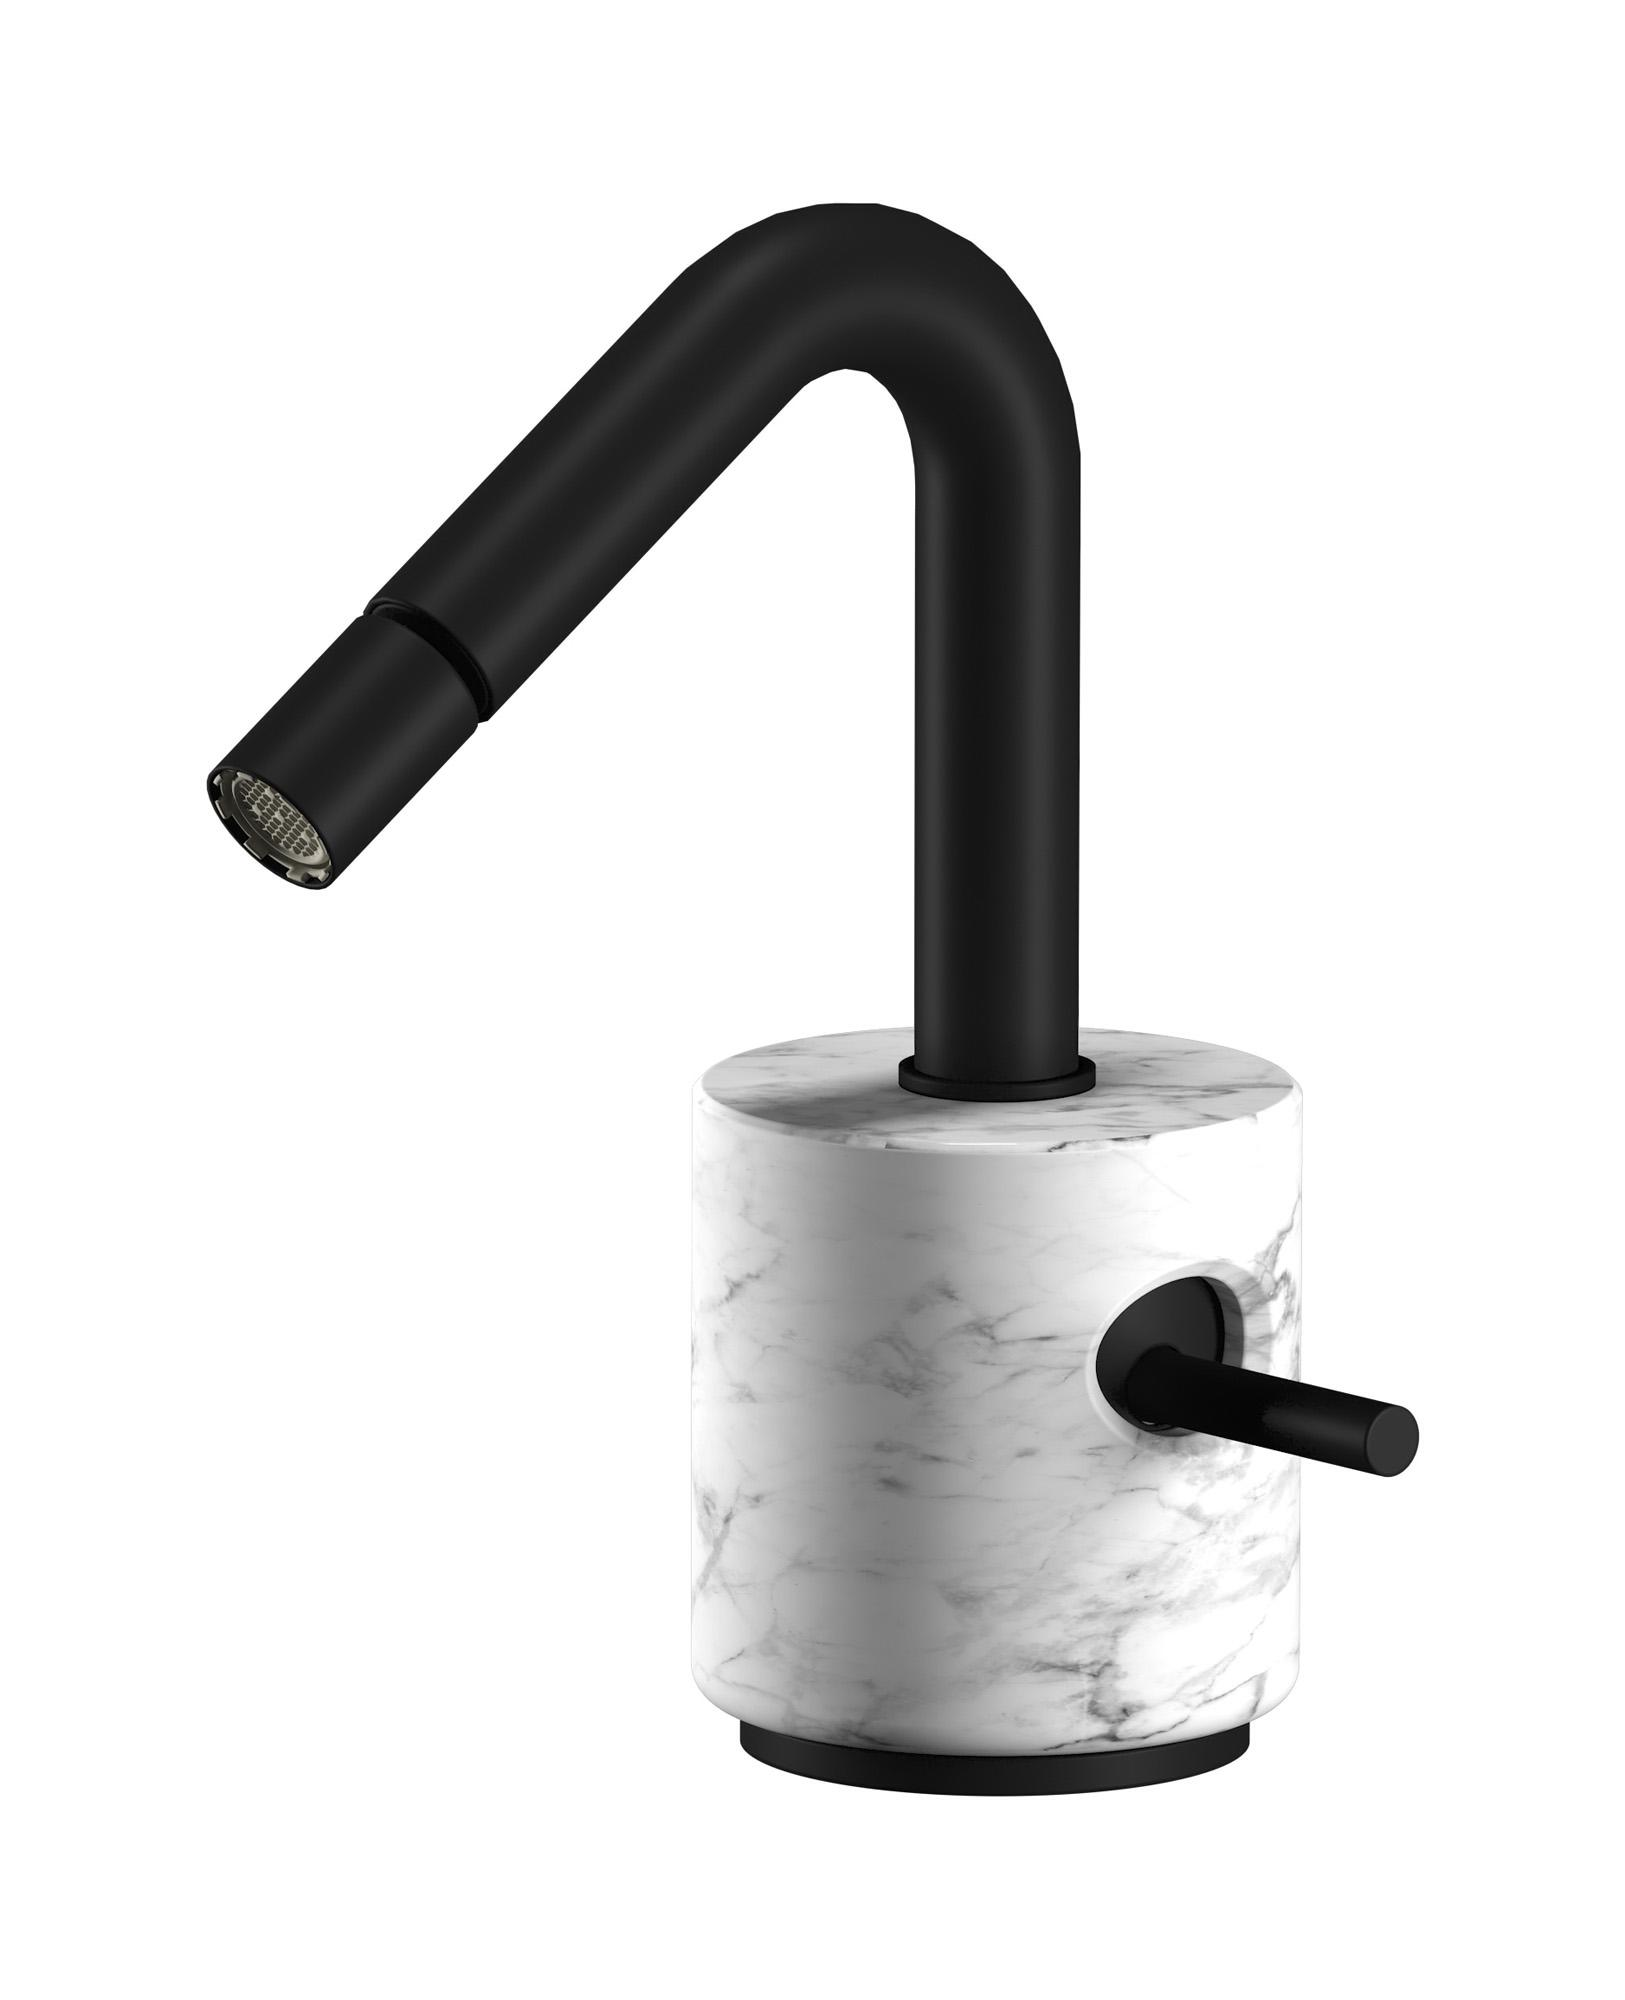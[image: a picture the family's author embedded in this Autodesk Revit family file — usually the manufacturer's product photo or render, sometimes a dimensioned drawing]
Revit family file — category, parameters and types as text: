
# Revit family: MR220_1
name_source: partatom
category: Apparecchi idraulici
units: mm (PartAtom-declared; Revit-internal decimal feet)

## family parameters
Basato su piano di lavoro = No
Condiviso = No
Mantieni orientamento annotazione = No
Numero OmniClass = 23.45.55.17
Punto di calcolo locali = No
Quota connettore circolare = Usa diametro
Sempre verticale = Sì
Taglio con vuoti quando caricato = No
Tipo di parte = Normale
Titolo OmniClass = Mixing Faucets

## types (14) — shared parameters
Cold water inlet = 10 mm  [stored 0.0328084 ft]
Commenti sul tipo = Bidet mixer
Connessione CW = No
Connessione HW = No
Connessione di scarico = No
Connessione di ventilazione = No
Descrizione = Monohole bidet mixer
Hot water inlet = 10 mm  [stored 0.0328084 ft]
Produttore = IB Rubinetterie S.p.A.
URL = https://www.weareib.it
zero-valued in all types: Prospetto di default

## per-type parameters (varying)
| type | Finishes surface | Immagine tipo | Modello |
| Chrome | IB_Chrome | MR220CC_1.jpg | MR220CC_1 |
| Platinum | IB_Platinum | MR220PL_1.jpg | MR220PL_1 |
| Brushed nickel | IB_Platinum | MR220SS_1.jpg | MR220SS_1 |
| Natural brass | IB_Brass | MR220ON_1.jpg | MR220ON_1 |
| Matt white | IB_matt white | MR220BO_1.jpg | MR220BO_1 |
| Matt black | IB_matt black | MR220NP_1.jpg | MR220NP_1 |
| Black chrome | IB_Black chrome | MR220CF_1.jpg | MR220CF_1 |
| Brushed black chrome | IB_Brushed black chrome | MR220CS_1.jpg | MR220CS_1 |
| Pale gold | IB_Pale gold | MR220II_1.jpg | MR220II_1 |
| Brushed pale gold | IB_brushed pale gold | MR220IS_1.jpg | MR220IS_1 |
| Rose gold | IB_Rose gold | MR220RS_1.jpg | MR220RS_1 |
| Brushed rose gold | IB_Brushed rose gold | MR220SR_1.jpg | MR220SR_1 |
| Gold | IB_gold | MR220OO_1.jpg | MR220OO_1 |
| Brushed gold | IB_brushed gold | MR220OS_1.jpg | MR220OS_1 |

note: [stored X ft] marks values corroborated as IEEE doubles in the binary element streams (Revit-internal decimal feet)
